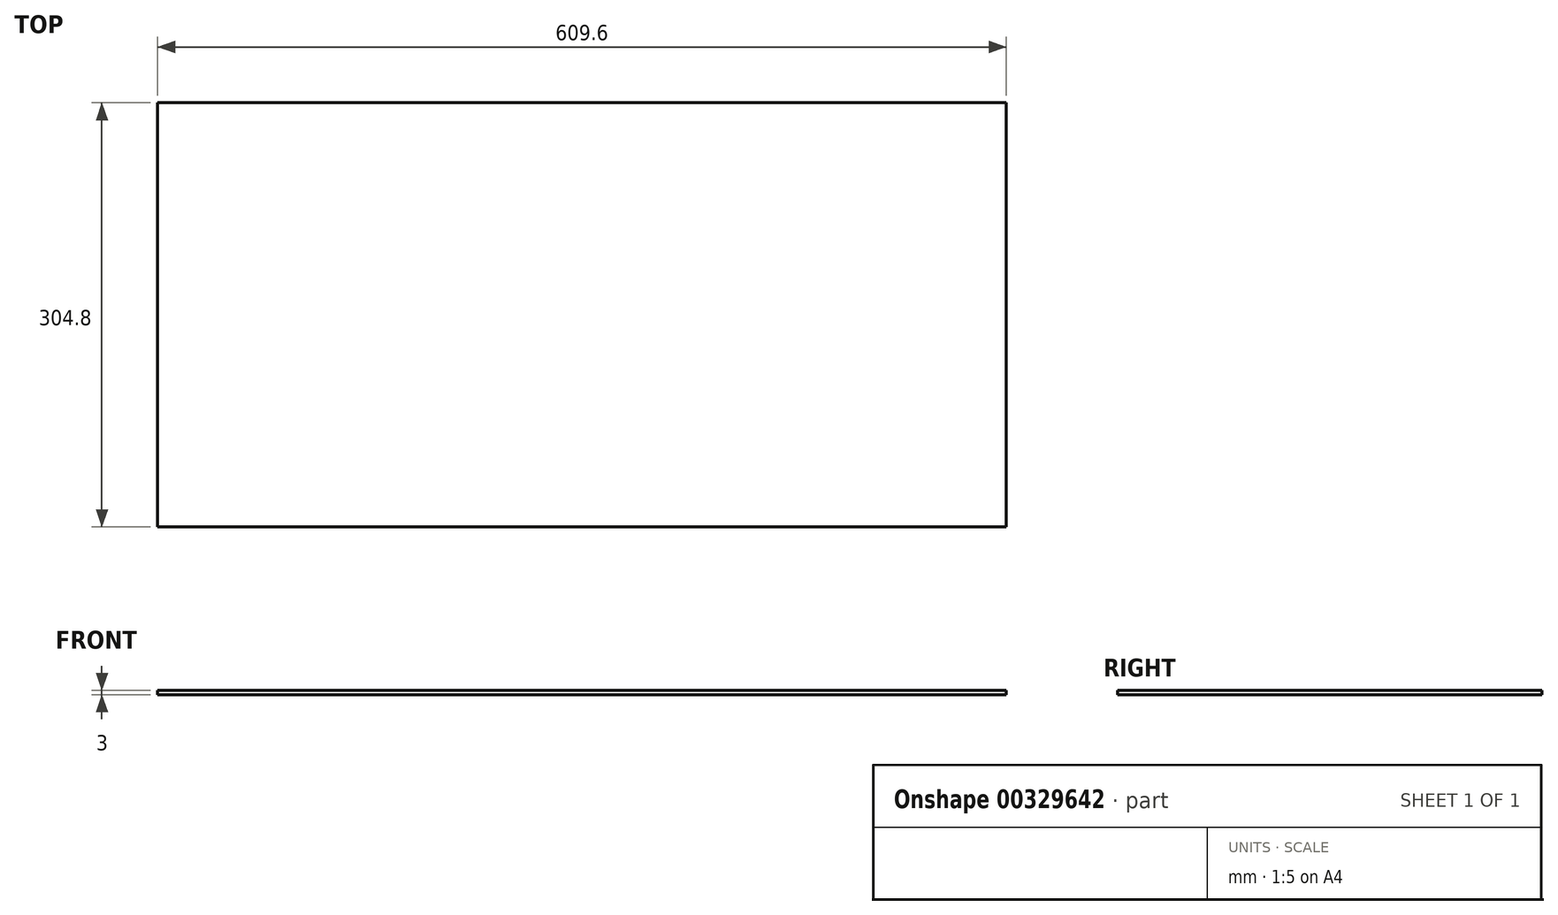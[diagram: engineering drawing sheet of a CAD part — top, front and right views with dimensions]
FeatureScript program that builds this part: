
annotation { "Feature Type Name" : "Feature", "Feature Type Description" : "" }
export const myFeature = defineFeature(function(context is Context, id is Id, definition is map)
    precondition{}
    {
        {
            var Q0;
            Q0=qCreatedBy(makeId("Top.planeOp"),FACE);
            var sketch = newSketch(context, id + "F0", { "sketchPlane" : qUnion([Q0])});
            skLineSegment(sketch, "E0.bottom", {"start": v(304.8, -152.4) * mm, "end": v(-304.8, -152.4) * mm});
            skLineSegment(sketch, "E0.top", {"start": v(304.8, 152.4) * mm, "end": v(-304.8, 152.4) * mm});
            skLineSegment(sketch, "E0.left", {"start": v(304.8, -152.4) * mm, "end": v(304.8, 152.4) * mm});
            skLineSegment(sketch, "E0.right", {"start": v(-304.8, -152.4) * mm, "end": v(-304.8, 152.4) * mm});
            skPoint(sketch, "E0.middle", {"position": v(0, 0) * mm});
            skSolve(sketch);
        }
        {
            var Q0;
            Q0 = qSketchRegion(id + "F0", true);
            extrude(context, id + "F1", {"entities" : qUnion([Q0]), "depth" : 3 * mm});
        }
    });
